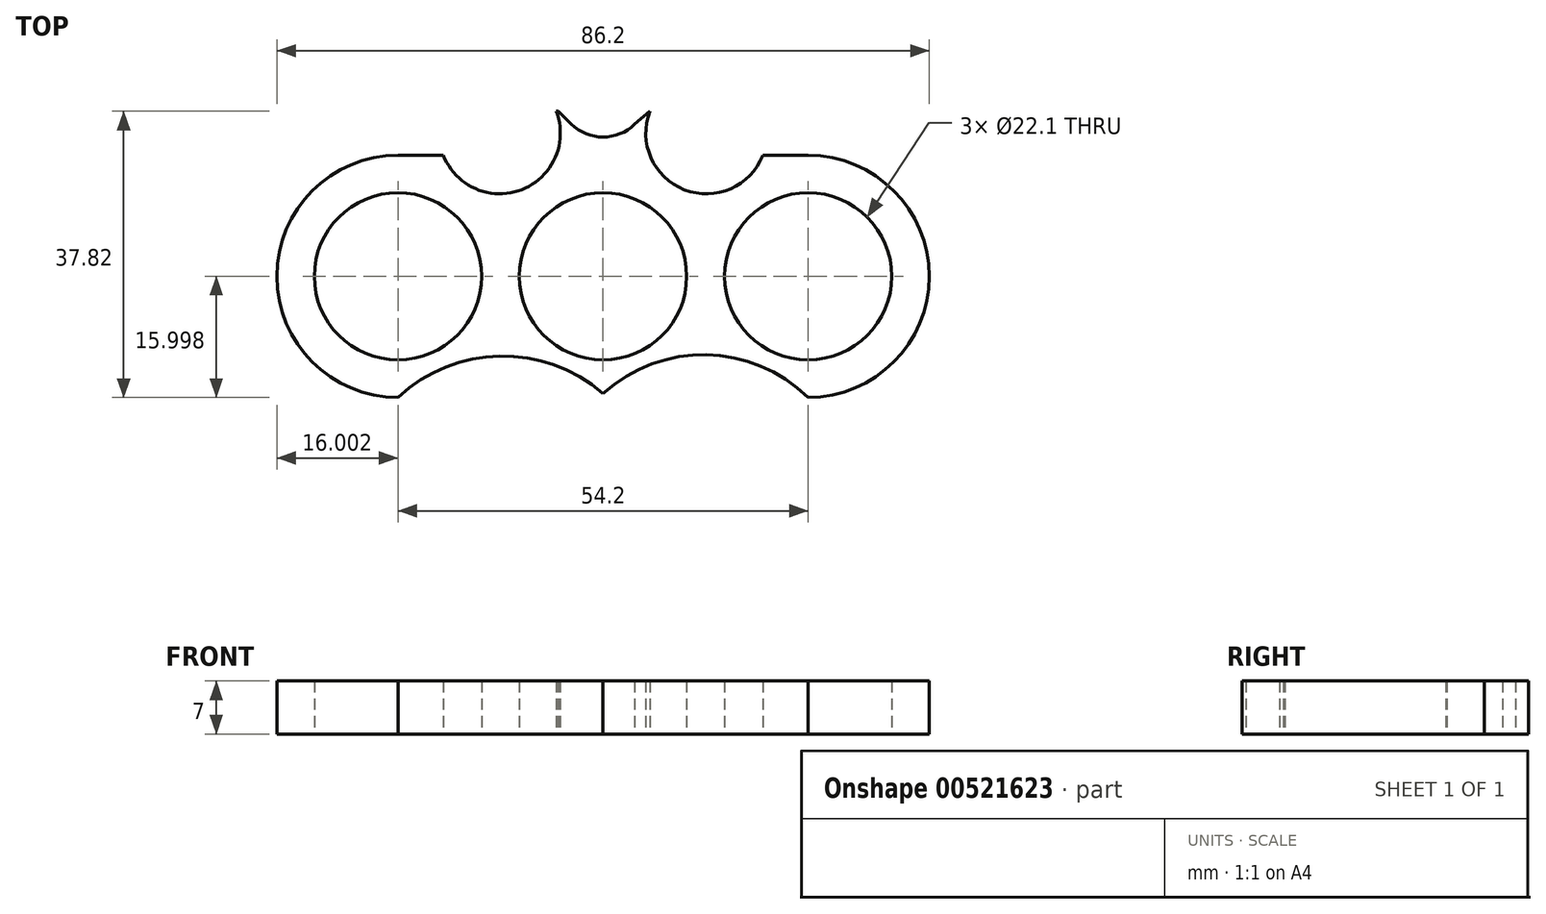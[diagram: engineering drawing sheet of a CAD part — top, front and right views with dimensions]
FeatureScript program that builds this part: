
annotation { "Feature Type Name" : "Feature", "Feature Type Description" : "" }
export const myFeature = defineFeature(function(context is Context, id is Id, definition is map)
    precondition{}
    {
        {
            var Q0;
            Q0=qCreatedBy(makeId("Top.planeOp"),FACE);
            var sketch = newSketch(context, id + "F0", { "sketchPlane" : qUnion([Q0])});
            skCircle(sketch, "E0", {"center": v(-8.18, 3.3) * mm, "radius": 11.05 * mm});
            skCircle(sketch, "E1", {"center": v(-35.28, 3.3) * mm, "radius": 11.05 * mm});
            skCircle(sketch, "E2", {"center": v(18.92, 3.3) * mm, "radius": 11.05 * mm});
            skCircle(sketch, "E3", {"center": v(-35.28, 3.3) * mm, "radius": 16 * mm});
            skCircle(sketch, "E4", {"center": v(18.92, 3.3) * mm, "radius": 16 * mm});
            skPoint(sketch, "E5.startSnap0", {"position": v(-19.23, -4.4) * mm});
            skArc(sketch, "E6", {"start": v(-8.18, -12.2) * mm, "mid": v(-21.82, -7.24) * mm, "end": v(-35.28, -12.7) * mm});
            skArc(sketch, "E7", {"start": v(18.92, -12.7) * mm, "mid": v(5.47, -7.07) * mm, "end": v(-8.18, -12.2) * mm});
            skLineSegment(sketch, "E8", {"start": v(-35.28, 19.3) * mm, "end": v(18.92, 19.3) * mm});
            skPoint(sketch, "E9.startSnap0", {"position": v(-21.82, -7.24) * mm});
            skPoint(sketch, "E9.endSnap0", {"position": v(-21.82, -7.24) * mm});
            skPoint(sketch, "E10.startSnap0", {"position": v(5.47, -7.07) * mm});
            skArc(sketch, "E11", {"start": v(-1.98, 25.12) * mm, "mid": v(2.56, 14.76) * mm, "end": v(12.92, 19.3) * mm});
            skPoint(sketch, "E12.startSnap0", {"position": v(-8.18, 19.3) * mm});
            skPoint(sketch, "E12.centerSnap0", {"position": v(-8.18, 19.3) * mm});
            skCircle(sketch, "E13", {"center": v(-21.82, 22.2) * mm, "radius": 8 * mm});
            skPoint(sketch, "E14.0.midPoint", {"position": v(-14.37, 25.12) * mm});
            skPoint(sketch, "E15.0.midPoint", {"position": v(-3.98, 25.12) * mm});
            skPoint(sketch, "E16.endSnap0", {"position": v(-12.37, 25.12) * mm});
            skLineSegment(sketch, "E17", {"start": v(-14.37, 25.12) * mm, "end": v(-12.37, 25.12) * mm});
            skLineSegment(sketch, "E18", {"start": v(-3.98, 25.12) * mm, "end": v(-1.98, 25.12) * mm});
            skArc(sketch, "E19", {"start": v(-12.37, 25.12) * mm, "mid": v(-8.18, 23.41) * mm, "end": v(-3.98, 25.12) * mm});
            skPoint(sketch, "E20.endSnap0", {"position": v(-8.18, 23.41) * mm});
            skArc(sketch, "E21", {"start": v(-12.37, 23.43) * mm, "mid": v(-8.18, 21.7) * mm, "end": v(-3.98, 23.41) * mm});
            skLineSegment(sketch, "E22", {"start": v(-12.37, 23.43) * mm, "end": v(-14.1, 25.12) * mm});
            skLineSegment(sketch, "E23", {"start": v(-3.98, 23.41) * mm, "end": v(-1.98, 25.12) * mm});
            skSolve(sketch);
        }
        {
            var Q0;
            Q0=makeQuery(id+"F0.imprint","IMPRINT",FACE,{"disambiguationData":[TD([[makeQuery(id+"F0.imprint","IMPRINT",EDGE,{"derivedFrom":sQuery(id+"F0.wireOp",EDGE,"E0")}),-1.0]])]});
            var Q1;
            Q1=makeQuery(id+"F0.imprint","IMPRINT",FACE,{"disambiguationData":[TD([[makeQuery(id+"F0.imprint","IMPRINT",EDGE,{"derivedFrom":sQuery(id+"F0.wireOp",EDGE,"E1")}),-1.0]])]});
            var Q2;
            Q2=makeQuery(id+"F0.imprint","IMPRINT",FACE,{"disambiguationData":[TD([[makeQuery(id+"F0.imprint","IMPRINT",EDGE,{"derivedFrom":sQuery(id+"F0.wireOp",EDGE,"E2")}),-1.0]])]});
            var Q3;
            {var subQ0=sQuery(id+"F0.wireOp",EDGE,"E8");var subQ1=sQuery(id+"F0.wireOp",EDGE,"E3");var subQ2=makeQuery(id+"F0.imprint","INTERSECT",VERTEX,{"derivedFrom":[subQ1,subQ0]});Q3=makeQuery(id+"F0.imprint","IMPRINT",FACE,{"disambiguationData":[TD([[makeQuery(id+"F0.imprint","IMPRINT",EDGE,{"disambiguationData":[TD([[subQ2,1.0]])],"derivedFrom":subQ1}),-1.0]])]});}
            var Q4;
            {var subQ0=sQuery(id+"F0.wireOp",EDGE,"E8");var subQ1=sQuery(id+"F0.wireOp",EDGE,"E4");var subQ2=makeQuery(id+"F0.imprint","INTERSECT",VERTEX,{"derivedFrom":[subQ1,subQ0]});Q4=makeQuery(id+"F0.imprint","IMPRINT",FACE,{"disambiguationData":[TD([[makeQuery(id+"F0.imprint","IMPRINT",EDGE,{"disambiguationData":[TD([[subQ2,-1.0]])],"derivedFrom":subQ1}),-1.0]])]});}
            var Q5;
            Q5=makeQuery(id+"F0.imprint","IMPRINT",FACE,{"disambiguationData":[TD([[makeQuery(id+"F0.imprint","IMPRINT",EDGE,{"derivedFrom":sQuery(id+"F0.wireOp",EDGE,"NQ7OtDZG-srIR-Cc7P-1aXZ-hOfXEOTmILGg")}),1.0]])]});
            var Q6;
            {var subQ3=sQuery(id+"F0.wireOp",EDGE,"ZraAqKGB-noOz-OMDO-dLHk-mEAV9DiwoPef");Q6=makeQuery(id+"F0.imprint","IMPRINT",FACE,{"disambiguationData":[TD([[makeQuery(id+"F0.imprint","IMPRINT",EDGE,{"derivedFrom":subQ3}),-1.0]])]});}
            var Q7;
            Q7=makeQuery(id+"F0.imprint","IMPRINT",FACE,{"disambiguationData":[TD([[makeQuery(id+"F0.imprint","IMPRINT",EDGE,{"derivedFrom":sQuery(id+"F0.wireOp",EDGE,"FL9tUTkg-SCTB-kFy6-flC4-0CjiKeXF2raQ")}),-1.0]])]});
            var Q8;
            Q8=makeQuery(id+"F0.imprint","IMPRINT",FACE,{"disambiguationData":[TD([[makeQuery(id+"F0.imprint","IMPRINT",EDGE,{"derivedFrom":sQuery(id+"F0.wireOp",EDGE,"E21")}),-1.0]])]});
            extrude(context, id + "F1", {"entities" : qUnion([Q0, Q1, Q2, Q3, Q4, Q5, Q6, Q7, Q8]), "depth" : 7 * mm, "offsetDistance" : 25 * mm});
        }
    });
